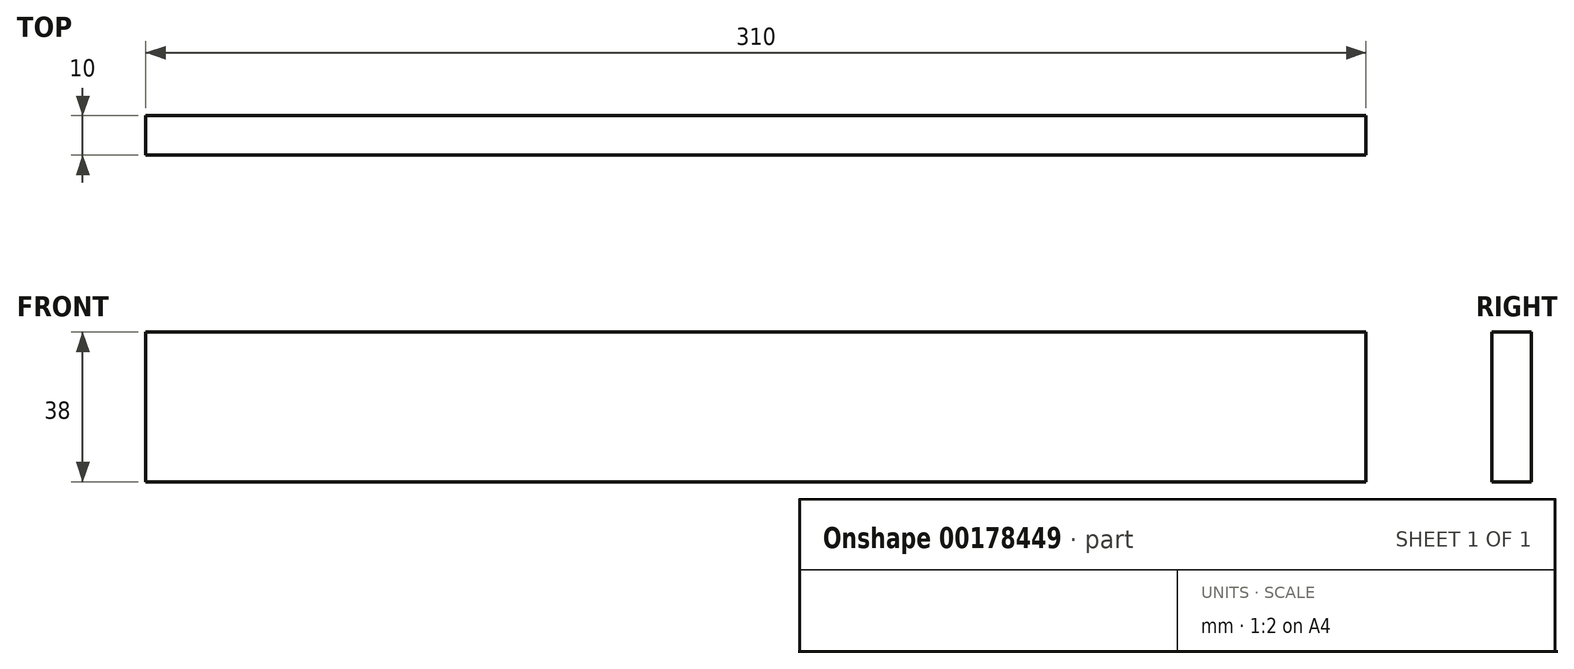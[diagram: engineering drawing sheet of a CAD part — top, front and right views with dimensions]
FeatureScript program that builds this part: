
annotation { "Feature Type Name" : "Feature", "Feature Type Description" : "" }
export const myFeature = defineFeature(function(context is Context, id is Id, definition is map)
    precondition{}
    {
        {
            var Q0;
            Q0=qCreatedBy(makeId("Front.planeOp"),FACE);
            var sketch = newSketch(context, id + "F0", { "sketchPlane" : qUnion([Q0])});
            skLineSegment(sketch, "E0.bottom", {"start": v(0, 0) * mm, "end": v(310, 0) * mm});
            skLineSegment(sketch, "E0.top", {"start": v(0, 38) * mm, "end": v(310, 38) * mm});
            skLineSegment(sketch, "E0.left", {"start": v(0, 0) * mm, "end": v(0, 38) * mm});
            skLineSegment(sketch, "E0.right", {"start": v(310, 0) * mm, "end": v(310, 38) * mm});
            skSolve(sketch);
        }
        {
            var Q0;
            Q0 = qSketchRegion(id + "F0", true);
            extrude(context, id + "F1", {"entities" : qUnion([Q0]), "depth" : 10 * mm});
        }
    });
